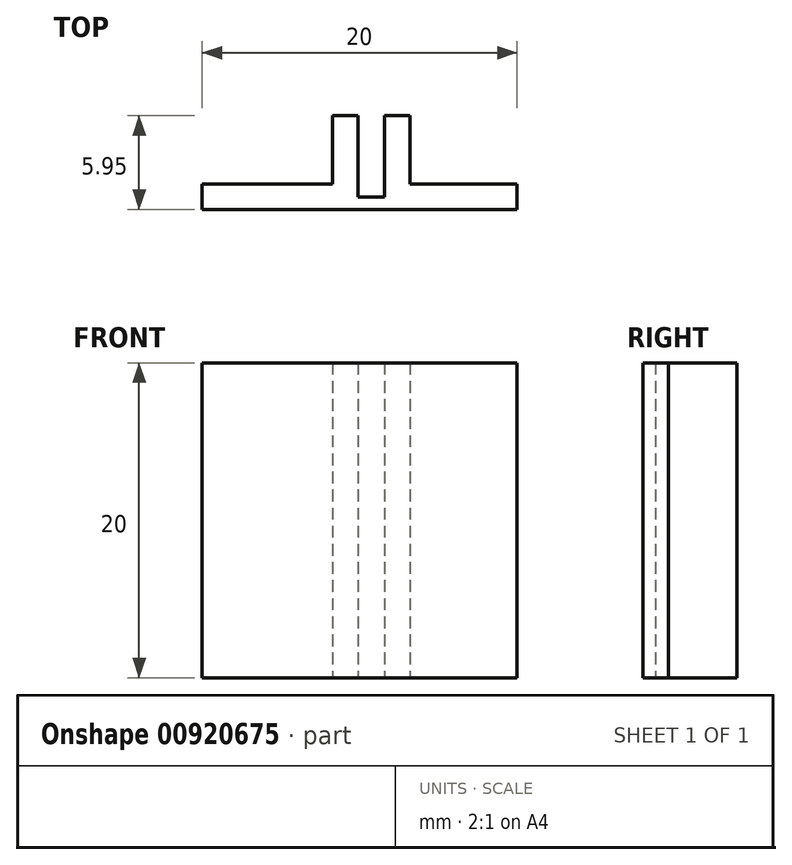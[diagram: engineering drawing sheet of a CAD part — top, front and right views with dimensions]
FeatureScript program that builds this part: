
annotation { "Feature Type Name" : "Feature", "Feature Type Description" : "" }
export const myFeature = defineFeature(function(context is Context, id is Id, definition is map)
    precondition{}
    {
        {
            var Q0;
            Q0=qCreatedBy(makeId("Top.planeOp"),FACE);
            var sketch = newSketch(context, id + "F0", { "sketchPlane" : qUnion([Q0])});
            skLineSegment(sketch, "E0", {"start": v(9.26, 0) * mm, "end": v(9.26, 0) * mm});
            skLineSegment(sketch, "E1", {"start": v(9.26, -1.6) * mm, "end": v(-10.74, -1.6) * mm});
            skLineSegment(sketch, "E2", {"start": v(-10.74, -1.6) * mm, "end": v(-10.74, 0) * mm});
            skLineSegment(sketch, "E3", {"start": v(-10.74, 0) * mm, "end": v(-10.74, 0) * mm});
            skLineSegment(sketch, "E4", {"start": v(-0.85, 0) * mm, "end": v(-0.85, -0.8) * mm});
            skLineSegment(sketch, "E5", {"start": v(-0.85, -0.8) * mm, "end": v(0.85, -0.8) * mm});
            skLineSegment(sketch, "E6", {"start": v(0.85, -0.8) * mm, "end": v(0.85, 0) * mm});
            skLineSegment(sketch, "E7", {"start": v(0.85, 0) * mm, "end": v(0.85, 4.35) * mm});
            skLineSegment(sketch, "E8", {"start": v(0.85, 4.35) * mm, "end": v(2.45, 4.35) * mm});
            skLineSegment(sketch, "E9", {"start": v(2.45, 4.35) * mm, "end": v(2.45, 0) * mm});
            skLineSegment(sketch, "E10", {"start": v(-0.85, 0) * mm, "end": v(-0.85, 0) * mm});
            skLineSegment(sketch, "E11", {"start": v(-0.85, 4.35) * mm, "end": v(-2.45, 4.35) * mm});
            skLineSegment(sketch, "E12", {"start": v(-2.45, 4.35) * mm, "end": v(-2.45, 0) * mm});
            skLineSegment(sketch, "E13", {"start": v(-10.74, 0) * mm, "end": v(-2.45, 0) * mm});
            skLineSegment(sketch, "E14", {"start": v(0.85, 0) * mm, "end": v(0.85, 0) * mm});
            skLineSegment(sketch, "E15", {"start": v(9.26, 0) * mm, "end": v(9.26, -1.6) * mm});
            skLineSegment(sketch, "E16", {"start": v(2.45, 0) * mm, "end": v(9.26, 0) * mm});
            skLineSegment(sketch, "E17", {"start": v(-0.85, 0) * mm, "end": v(-0.85, 4.35) * mm});
            skSolve(sketch);
        }
        {
            var Q0;
            Q0=makeQuery(id+"F0.imprint","IMPRINT",FACE,{"disambiguationData":[TD([[makeQuery(id+"F0.imprint","IMPRINT",EDGE,{"derivedFrom":sQuery(id+"F0.wireOp",EDGE,"E1")}),-1.0]])]});
            extrude(context, id + "F1", {"entities" : qUnion([Q0]), "depth" : 20 * mm, "offsetDistance" : 25 * mm});
        }
    });
